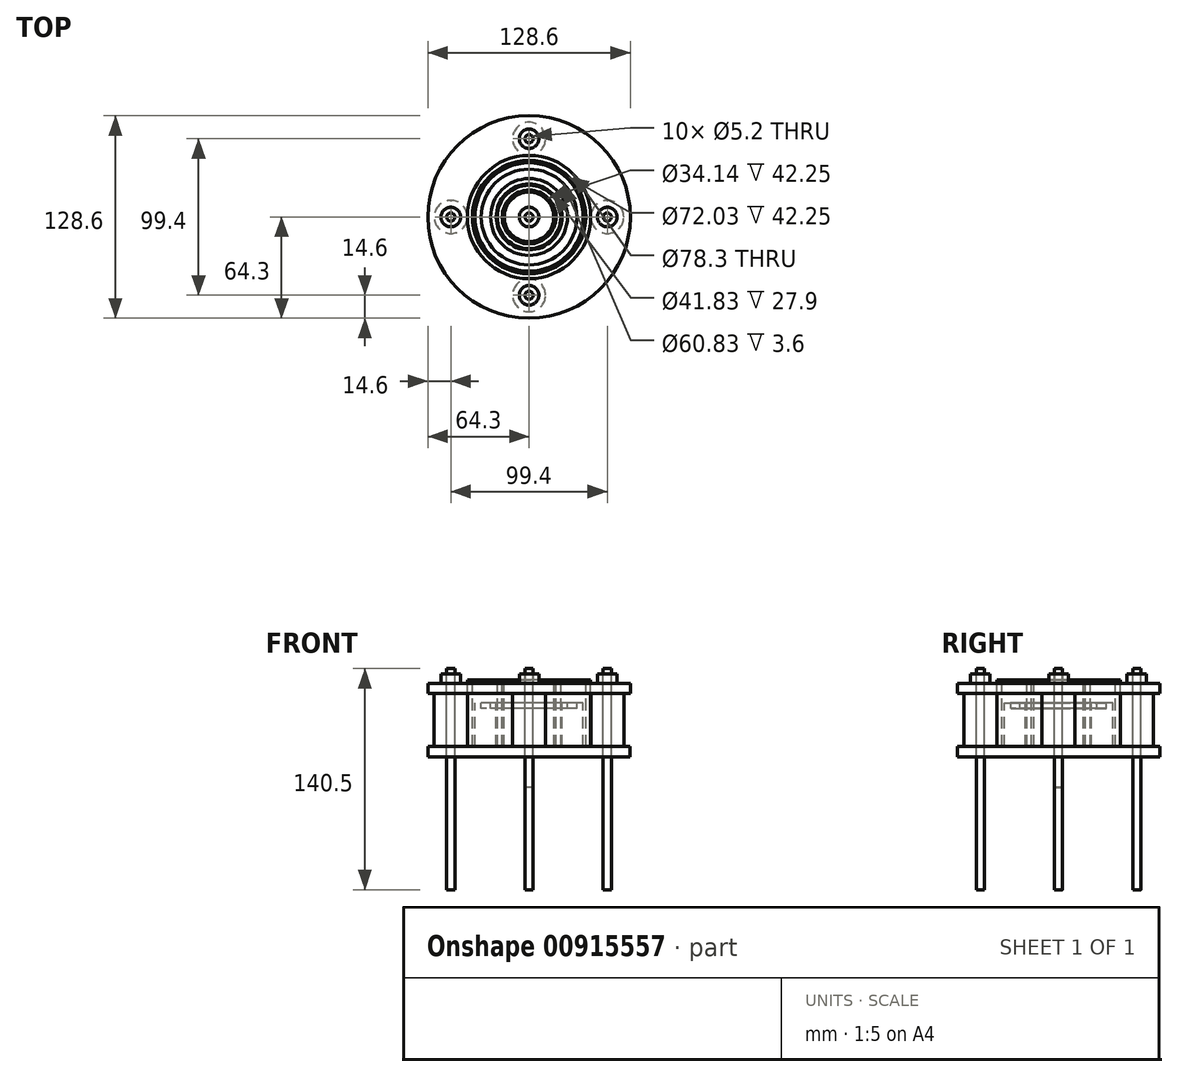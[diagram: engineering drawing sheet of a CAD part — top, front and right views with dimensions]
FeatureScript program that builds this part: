
annotation { "Feature Type Name" : "Feature", "Feature Type Description" : "" }
export const myFeature = defineFeature(function(context is Context, id is Id, definition is map)
    precondition{}
    {
        {
            var Q0;
            Q0=qCreatedBy(makeId("Top.planeOp"),FACE);
            var sketch = newSketch(context, id + "F0", { "sketchPlane" : qUnion([Q0])});
            skCircle(sketch, "E0", {"center": v(0, 0) * mm, "radius": 64.3 * mm});
            skCircle(sketch, "E1", {"center": v(0, 0) * mm, "radius": 39.15 * mm});
            skCircle(sketch, "E2", {"center": v(0, 0) * mm, "radius": 36.02 * mm});
            skCircle(sketch, "E3", {"center": v(0, 0) * mm, "radius": 20.15 * mm});
            skCircle(sketch, "E4", {"center": v(0, 0) * mm, "radius": 17.07 * mm});
            skCircle(sketch, "E5", {"center": v(0, 0) * mm, "radius": 15.75 * mm});
            skPoint(sketch, "E6", {"position": v(0, 64.3) * mm});
            skPoint(sketch, "E7", {"position": v(-64.3, 0) * mm});
            skPoint(sketch, "E8", {"position": v(64.3, 0) * mm});
            skPoint(sketch, "E9", {"position": v(-49.7, 0) * mm});
            skPoint(sketch, "E10", {"position": v(0, 49.7) * mm});
            skPoint(sketch, "E11", {"position": v(49.7, 0) * mm});
            skCircle(sketch, "E12", {"center": v(-49.7, 0) * mm, "radius": 6.2 * mm});
            skCircle(sketch, "E13", {"center": v(0, -49.7) * mm, "radius": 6.2 * mm});
            skCircle(sketch, "E14", {"center": v(49.7, 0) * mm, "radius": 6.2 * mm});
            skCircle(sketch, "E15", {"center": v(0, 49.7) * mm, "radius": 6.2 * mm});
            skPoint(sketch, "E16", {"position": v(0, -64.3) * mm});
            skCircle(sketch, "E17", {"center": v(0, 0) * mm, "radius": 34.41 * mm});
            skPoint(sketch, "E18", {"position": v(-36.02, 0) * mm});
            skPoint(sketch, "E19", {"position": v(-34.41, 0) * mm});
            skCircle(sketch, "E20", {"center": v(0, 0) * mm, "radius": 30.42 * mm});
            skPoint(sketch, "E21", {"position": v(-30.42, 0) * mm});
            skCircle(sketch, "E22", {"center": v(0, 0) * mm, "radius": 24.41 * mm});
            skCircle(sketch, "E23", {"center": v(0, 0) * mm, "radius": 20.91 * mm});
            skPoint(sketch, "E24", {"position": v(-24.41, 0) * mm});
            skPoint(sketch, "E25", {"position": v(-20.91, 0) * mm});
            skCircle(sketch, "E26", {"center": v(-49.7, 0) * mm, "radius": 10.5 * mm});
            skCircle(sketch, "E27", {"center": v(0, 49.7) * mm, "radius": 10.5 * mm});
            skCircle(sketch, "E28", {"center": v(49.7, 0) * mm, "radius": 10.5 * mm});
            skCircle(sketch, "E29", {"center": v(0, -49.7) * mm, "radius": 10.5 * mm});
            skCircle(sketch, "E30", {"center": v(-49.7, 0) * mm, "radius": 2.6 * mm});
            skCircle(sketch, "E31", {"center": v(0, -49.7) * mm, "radius": 2.6 * mm});
            skCircle(sketch, "E32", {"center": v(49.7, 0) * mm, "radius": 2.6 * mm});
            skCircle(sketch, "E33", {"center": v(0, 49.7) * mm, "radius": 2.6 * mm});
            skCircle(sketch, "E34", {"center": v(0, 0) * mm, "radius": 6.2 * mm});
            skCircle(sketch, "E35", {"center": v(0, 0) * mm, "radius": 2.6 * mm});
            skSolve(sketch);
        }
        {
            var Q0;
            Q0=makeQuery(id+"F0.imprint","IMPRINT",FACE,{"disambiguationData":[TD([[makeQuery(id+"F0.imprint","IMPRINT",EDGE,{"derivedFrom":sQuery(id+"F0.wireOp",EDGE,"E13")}),1.0]])]});
            var Q1;
            Q1=makeQuery(id+"F0.imprint","IMPRINT",FACE,{"disambiguationData":[TD([[makeQuery(id+"F0.imprint","IMPRINT",EDGE,{"derivedFrom":sQuery(id+"F0.wireOp",EDGE,"E13")}),-1.0]])]});
            var Q2;
            Q2=makeQuery(id+"F0.imprint","IMPRINT",FACE,{"disambiguationData":[TD([[makeQuery(id+"F0.imprint","IMPRINT",EDGE,{"derivedFrom":sQuery(id+"F0.wireOp",EDGE,"E0")}),1.0]])]});
            var Q3;
            Q3=makeQuery(id+"F0.imprint","IMPRINT",FACE,{"disambiguationData":[TD([[makeQuery(id+"F0.imprint","IMPRINT",EDGE,{"derivedFrom":sQuery(id+"F0.wireOp",EDGE,"E14")}),-1.0]])]});
            var Q4;
            Q4=makeQuery(id+"F0.imprint","IMPRINT",FACE,{"disambiguationData":[TD([[makeQuery(id+"F0.imprint","IMPRINT",EDGE,{"derivedFrom":sQuery(id+"F0.wireOp",EDGE,"E14")}),1.0]])]});
            var Q5;
            Q5=makeQuery(id+"F0.imprint","IMPRINT",FACE,{"disambiguationData":[TD([[makeQuery(id+"F0.imprint","IMPRINT",EDGE,{"derivedFrom":sQuery(id+"F0.wireOp",EDGE,"E15")}),-1.0]])]});
            var Q6;
            Q6=makeQuery(id+"F0.imprint","IMPRINT",FACE,{"disambiguationData":[TD([[makeQuery(id+"F0.imprint","IMPRINT",EDGE,{"derivedFrom":sQuery(id+"F0.wireOp",EDGE,"E15")}),1.0]])]});
            var Q7;
            Q7=makeQuery(id+"F0.imprint","IMPRINT",FACE,{"disambiguationData":[TD([[makeQuery(id+"F0.imprint","IMPRINT",EDGE,{"derivedFrom":sQuery(id+"F0.wireOp",EDGE,"E12")}),-1.0]])]});
            var Q8;
            Q8=makeQuery(id+"F0.imprint","IMPRINT",FACE,{"disambiguationData":[TD([[makeQuery(id+"F0.imprint","IMPRINT",EDGE,{"derivedFrom":sQuery(id+"F0.wireOp",EDGE,"E12")}),1.0]])]});
            extrude(context, id + "F1", {"entities" : qUnion([Q0, Q1, Q2, Q3, Q4, Q5, Q6, Q7, Q8]), "oppositeDirection" : true, "depth" : 6.4 * mm, "offsetDistance" : 25 * mm});
        }
        {
            var Q0;
            Q0=makeQuery(id+"F0.imprint","IMPRINT",FACE,{"disambiguationData":[TD([[makeQuery(id+"F0.imprint","IMPRINT",EDGE,{"derivedFrom":sQuery(id+"F0.wireOp",EDGE,"E1")}),1.0]])]});
            extrude(context, id + "F2", {"entities" : qUnion([Q0]), "oppositeDirection" : true, "depth" : 46.5 * mm, "offsetDistance" : 25 * mm, "hasSecondDirection" : true, "secondDirectionOppositeDirection" : false, "secondDirectionDepth" : 2.15 * mm});
        }
        {
            var Q0;
            Q0=makeQuery(id+"F2.opExtrude","CAP_FACE",FACE,{"disambiguationData":[OSD([sQuery(id+"F0.wireOp",EDGE,"E1"),sQuery(id+"F0.wireOp",EDGE,"E2")])],"isStart":false});
            var sketch = newSketch(context, id + "F3", { "sketchPlane" : qUnion([Q0])});
            skCircle(sketch, "E36", {"center": v(0, 0) * mm, "radius": 64.2 * mm});
            skSolve(sketch);
        }
        {
            var Q0;
            Q0=makeQuery(id+"F3.imprint","IMPRINT",FACE,{"disambiguationData":[TD([[makeQuery(id+"F3.imprint","IMPRINT",EDGE,{"derivedFrom":sQuery(id+"F3.wireOp",EDGE,"E36")}),1.0]])]});
            var Q1;
            Q1=makeQuery(id+"F3.imprint","IMPRINT",FACE,{"disambiguationData":[TD([[makeQuery(id+"F3.imprint","IMPRINT",EDGE,{"derivedFrom":makeQuery(id+"F2.opExtrude","CAP_EDGE",EDGE,{"disambiguationData":[OSD([sQuery(id+"F0.wireOp",EDGE,"E2")])],"isStart":false})}),-1.0]])]});
            extrude(context, id + "F4", {"entities" : qUnion([Q0, Q1]), "operationType" : NewBodyOperationType.ADD, "oppositeDirection" : true, "depth" : 6.4 * mm, "offsetDistance" : 25 * mm});
        }
        {
            var Q0;
            Q0=makeQuery(id+"F0.imprint","IMPRINT",FACE,{"disambiguationData":[TD([[makeQuery(id+"F0.imprint","IMPRINT",EDGE,{"derivedFrom":sQuery(id+"F0.wireOp",EDGE,"E3")}),1.0]])]});
            extrude(context, id + "F5", {"entities" : qUnion([Q0]), "oppositeDirection" : true, "depth" : 40.1 * mm, "offsetDistance" : 25 * mm, "hasSecondDirection" : true, "secondDirectionOppositeDirection" : false, "secondDirectionDepth" : 2.15 * mm});
        }
        {
            var Q0;
            Q0=makeQuery(id+"F0.imprint","IMPRINT",FACE,{"disambiguationData":[TD([[makeQuery(id+"F0.imprint","IMPRINT",EDGE,{"derivedFrom":sQuery(id+"F0.wireOp",EDGE,"E17")}),1.0]])]});
            var Q1;
            Q1=makeQuery(id+"F0.imprint","IMPRINT",FACE,{"disambiguationData":[TD([[makeQuery(id+"F0.imprint","IMPRINT",EDGE,{"derivedFrom":sQuery(id+"F0.wireOp",EDGE,"E20")}),1.0]])]});
            var Q2;
            Q2=makeQuery(id+"F0.imprint","IMPRINT",FACE,{"disambiguationData":[TD([[makeQuery(id+"F0.imprint","IMPRINT",EDGE,{"derivedFrom":sQuery(id+"F0.wireOp",EDGE,"E22")}),1.0]])]});
            extrude(context, id + "F6", {"entities" : qUnion([Q0, Q1, Q2]), "oppositeDirection" : true, "depth" : 40.1 * mm, "offsetDistance" : 25 * mm});
        }
        {
            var Q0;
            Q0=makeQuery(id+"F0.imprint","IMPRINT",FACE,{"disambiguationData":[TD([[makeQuery(id+"F0.imprint","IMPRINT",EDGE,{"derivedFrom":sQuery(id+"F0.wireOp",EDGE,"E17")}),1.0]])]});
            extrude(context, id + "F7", {"entities" : qUnion([Q0]), "operationType" : NewBodyOperationType.REMOVE, "oppositeDirection" : true, "depth" : 12.2 * mm, "offsetDistance" : 25 * mm});
        }
        {
            var Q0;
            Q0=makeQuery(id+"F0.imprint","IMPRINT",FACE,{"disambiguationData":[TD([[makeQuery(id+"F0.imprint","IMPRINT",EDGE,{"derivedFrom":sQuery(id+"F0.wireOp",EDGE,"E20")}),1.0]])]});
            extrude(context, id + "F8", {"entities" : qUnion([Q0]), "operationType" : NewBodyOperationType.REMOVE, "oppositeDirection" : true, "depth" : 15.8 * mm, "offsetDistance" : 25 * mm});
        }
        {
            var Q0;
            Q0=makeQuery(id+"F0.imprint","IMPRINT",FACE,{"disambiguationData":[TD([[makeQuery(id+"F0.imprint","IMPRINT",EDGE,{"derivedFrom":sQuery(id+"F0.wireOp",EDGE,"E22")}),1.0]])]});
            extrude(context, id + "F9", {"entities" : qUnion([Q0]), "operationType" : NewBodyOperationType.REMOVE, "oppositeDirection" : true, "depth" : 12.2 * mm, "offsetDistance" : 25 * mm});
        }
        {
            var Q0;
            Q0=makeQuery(id+"F0.imprint","IMPRINT",FACE,{"disambiguationData":[TD([[makeQuery(id+"F0.imprint","IMPRINT",EDGE,{"derivedFrom":sQuery(id+"F0.wireOp",EDGE,"E5")}),1.0]])]});
            var Q1;
            Q1=makeQuery(id+"F0.imprint","IMPRINT",FACE,{"disambiguationData":[TD([[makeQuery(id+"F0.imprint","IMPRINT",EDGE,{"derivedFrom":sQuery(id+"F0.wireOp",EDGE,"E34")}),1.0]])]});
            extrude(context, id + "F10", {"entities" : qUnion([Q0, Q1]), "oppositeDirection" : true, "depth" : 40.1 * mm, "offsetDistance" : 25 * mm, "hasSecondDirection" : true, "secondDirectionOppositeDirection" : true, "secondDirectionDepth" : 0.35 * mm});
        }
        {
            var Q0;
            Q0=makeQuery(id+"F0.imprint","IMPRINT",FACE,{"disambiguationData":[TD([[makeQuery(id+"F0.imprint","IMPRINT",EDGE,{"derivedFrom":sQuery(id+"F0.wireOp",EDGE,"E14")}),1.0]])]});
            var Q1;
            Q1=makeQuery(id+"F0.imprint","IMPRINT",FACE,{"disambiguationData":[TD([[makeQuery(id+"F0.imprint","IMPRINT",EDGE,{"derivedFrom":sQuery(id+"F0.wireOp",EDGE,"E13")}),1.0]])]});
            var Q2;
            Q2=makeQuery(id+"F0.imprint","IMPRINT",FACE,{"disambiguationData":[TD([[makeQuery(id+"F0.imprint","IMPRINT",EDGE,{"derivedFrom":sQuery(id+"F0.wireOp",EDGE,"E12")}),1.0]])]});
            var Q3;
            Q3=makeQuery(id+"F0.imprint","IMPRINT",FACE,{"disambiguationData":[TD([[makeQuery(id+"F0.imprint","IMPRINT",EDGE,{"derivedFrom":sQuery(id+"F0.wireOp",EDGE,"E15")}),1.0]])]});
            extrude(context, id + "F11", {"entities" : qUnion([Q0, Q1, Q2, Q3]), "operationType" : NewBodyOperationType.ADD, "depth" : 6 * mm, "offsetDistance" : 25 * mm});
        }
        {
            var Q0;
            Q0=makeQuery(id+"F0.imprint","IMPRINT",FACE,{"disambiguationData":[TD([[makeQuery(id+"F0.imprint","IMPRINT",EDGE,{"derivedFrom":sQuery(id+"F0.wireOp",EDGE,"E30")}),1.0]])]});
            var Q1;
            Q1=makeQuery(id+"F0.imprint","IMPRINT",FACE,{"disambiguationData":[TD([[makeQuery(id+"F0.imprint","IMPRINT",EDGE,{"derivedFrom":sQuery(id+"F0.wireOp",EDGE,"E33")}),1.0]])]});
            var Q2;
            Q2=makeQuery(id+"F0.imprint","IMPRINT",FACE,{"disambiguationData":[TD([[makeQuery(id+"F0.imprint","IMPRINT",EDGE,{"derivedFrom":sQuery(id+"F0.wireOp",EDGE,"E32")}),1.0]])]});
            var Q3;
            Q3=makeQuery(id+"F0.imprint","IMPRINT",FACE,{"disambiguationData":[TD([[makeQuery(id+"F0.imprint","IMPRINT",EDGE,{"derivedFrom":sQuery(id+"F0.wireOp",EDGE,"E31")}),1.0]])]});
            var Q4;
            Q4=sQuery(id+"F0.wireOp",EDGE,"E30");
            var Q5;
            Q5=sQuery(id+"F0.wireOp",EDGE,"E31");
            var Q6;
            Q6=sQuery(id+"F0.wireOp",EDGE,"E32");
            var Q7;
            Q7=sQuery(id+"F0.wireOp",EDGE,"E33");
            extrude(context, id + "F12", {"entities" : qUnion([Q0, Q1, Q2, Q3]), "surfaceEntities" : qUnion([Q4, Q5, Q6, Q7]), "oppositeDirection" : true, "depth" : 131 * mm, "offsetDistance" : 25 * mm, "hasSecondDirection" : true, "secondDirectionOppositeDirection" : false, "secondDirectionDepth" : 9.5 * mm});
        }
        {
            var Q0;
            Q0=makeQuery(id+"F0.imprint","IMPRINT",FACE,{"disambiguationData":[TD([[makeQuery(id+"F0.imprint","IMPRINT",EDGE,{"derivedFrom":sQuery(id+"F0.wireOp",EDGE,"E13")}),-1.0]])]});
            var Q1;
            Q1=makeQuery(id+"F0.imprint","IMPRINT",FACE,{"disambiguationData":[TD([[makeQuery(id+"F0.imprint","IMPRINT",EDGE,{"derivedFrom":sQuery(id+"F0.wireOp",EDGE,"E15")}),-1.0]])]});
            var Q2;
            Q2=makeQuery(id+"F0.imprint","IMPRINT",FACE,{"disambiguationData":[TD([[makeQuery(id+"F0.imprint","IMPRINT",EDGE,{"derivedFrom":sQuery(id+"F0.wireOp",EDGE,"E12")}),-1.0]])]});
            var Q3;
            Q3=makeQuery(id+"F0.imprint","IMPRINT",FACE,{"disambiguationData":[TD([[makeQuery(id+"F0.imprint","IMPRINT",EDGE,{"derivedFrom":sQuery(id+"F0.wireOp",EDGE,"E14")}),-1.0]])]});
            var Q4;
            Q4=makeQuery(id+"F0.imprint","IMPRINT",FACE,{"disambiguationData":[TD([[makeQuery(id+"F0.imprint","IMPRINT",EDGE,{"derivedFrom":sQuery(id+"F0.wireOp",EDGE,"E12")}),1.0]])]});
            var Q5;
            Q5=makeQuery(id+"F0.imprint","IMPRINT",FACE,{"disambiguationData":[TD([[makeQuery(id+"F0.imprint","IMPRINT",EDGE,{"derivedFrom":sQuery(id+"F0.wireOp",EDGE,"E13")}),1.0]])]});
            var Q6;
            Q6=makeQuery(id+"F0.imprint","IMPRINT",FACE,{"disambiguationData":[TD([[makeQuery(id+"F0.imprint","IMPRINT",EDGE,{"derivedFrom":sQuery(id+"F0.wireOp",EDGE,"E14")}),1.0]])]});
            var Q7;
            Q7=makeQuery(id+"F0.imprint","IMPRINT",FACE,{"disambiguationData":[TD([[makeQuery(id+"F0.imprint","IMPRINT",EDGE,{"derivedFrom":sQuery(id+"F0.wireOp",EDGE,"E15")}),1.0]])]});
            var Q8;
            Q8=sQuery(id+"F0.wireOp",EDGE,"E28");
            var Q9;
            Q9=sQuery(id+"F0.wireOp",EDGE,"E29");
            var Q10;
            Q10=sQuery(id+"F0.wireOp",EDGE,"E26");
            var Q11;
            Q11=sQuery(id+"F0.wireOp",EDGE,"E27");
            extrude(context, id + "F13", {"entities" : qUnion([Q0, Q1, Q2, Q3, Q4, Q5, Q6, Q7]), "surfaceEntities" : qUnion([Q8, Q9, Q10, Q11]), "oppositeDirection" : true, "depth" : 40.1 * mm, "offsetDistance" : 25 * mm, "hasSecondDirection" : true, "secondDirectionOppositeDirection" : true, "secondDirectionDepth" : 6.4 * mm});
        }
        {
            var Q0;
            Q0=makeQuery(id+"F0.imprint","IMPRINT",FACE,{"disambiguationData":[TD([[makeQuery(id+"F0.imprint","IMPRINT",EDGE,{"derivedFrom":sQuery(id+"F0.wireOp",EDGE,"E35")}),1.0]])]});
            var Q1;
            Q1=sQuery(id+"F0.wireOp",EDGE,"E35");
            extrude(context, id + "F14", {"entities" : qUnion([Q0]), "surfaceEntities" : qUnion([Q1]), "oppositeDirection" : true, "depth" : 65.9 * mm, "offsetDistance" : 25 * mm, "hasSecondDirection" : true, "secondDirectionOppositeDirection" : false, "secondDirectionDepth" : 9.5 * mm});
        }
        {
            var Q0;
            Q0=makeQuery(id+"F0.imprint","IMPRINT",FACE,{"disambiguationData":[TD([[makeQuery(id+"F0.imprint","IMPRINT",EDGE,{"derivedFrom":sQuery(id+"F0.wireOp",EDGE,"E34")}),1.0]])]});
            var Q1;
            Q1=sQuery(id+"F0.wireOp",EDGE,"E34");
            extrude(context, id + "F15", {"entities" : qUnion([Q0]), "surfaceEntities" : qUnion([Q1]), "depth" : 5.65 * mm, "offsetDistance" : 25 * mm, "hasSecondDirection" : true, "secondDirectionOppositeDirection" : true, "secondDirectionDepth" : 0.35 * mm});
        }
    });
